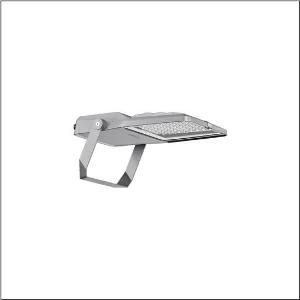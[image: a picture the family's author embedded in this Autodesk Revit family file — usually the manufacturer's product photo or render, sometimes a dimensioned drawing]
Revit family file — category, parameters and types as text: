
# Revit family: floodlight_fl_21_iq_mini___pl52_5xa7771d2d1a_936e
name_source: partatom
category: Lighting Fixtures
units: mm (PartAtom-declared; Revit-internal decimal feet)

## family parameters
Cut with Voids When Loaded = No
Host = Face
Light Source = No
Part Type = Normal
Room Calculation Point = No
Round Connector Dimension = Use Diameter
Shared = No

## types (1)
- --- (1 x LED, 17830 lm, 143 W, 3000K)
    Apparent Load = 143 VA
    CIE Flux Codes = 26 60 98 100 100
    Color Rendering = 70
    Color Temperature = 3000K
    Default Elevation = 1800 mm
    Description = Floodlight FL 21 iQ mini, floodlight, primary light control with lens, of PMMA, primary optical cover: protective disc, of toughened safety glass, transparent, light distribution: PL52, light emission: direct distribution, installation type: surface-mounted, LED, High Power LED, rated luminous flux: 17.830lm, luminous efficacy: 125lm/W, light colour: 730, colour temperature: 3000K, control: Auto-Match, Temp-Guard, Lumen-Switch, Night-Set, Smart-Wire, Light-Fading, Desk-Remote (wireless, voltage-free reading and setting of iQ features in the workshop via application-optimized NFC function/RFID function), optimised constant luminous flux control (CLO 2.0), with terminal, 6-pole, mains connection: 220..240V, AC, 50/60Hz, start of lifetime: 143W, end of service life: 152W, reduction: 61W, luminaire housing, of diecast aluminium, powder-coated, Siteco® metallic grey (DB 702S), corrosivity category C5 mid according to DIN EN ISO 12944, sealing non-destructively replaceable, mounting bracket, of steel, galvanised, powder-coated, Siteco® metallic grey (DB 702S), protection rating (complete): IP66, insulation class (complete): insulation class II (safety insulation), certification: CE, ENEC, VDE, protection symbol: D, impact resistance: IK08, permissible operating ambient temperature: -40..+40°C, permissible operating ambient temperature for outdoor applications: -40..+50°C, standard: DIN EN 12944, LABS conformity tested according to VDMA 24364:2018-05, packaging unit: 1 piece

Light Distribution: PL52
    Height = 70 mm
    Lamp = 1 x LED
    Lamp Light Flux = 17830 lm
    Lamp Power = 143 W
    Lamp count = 1
    Length = 485 mm
    Luminous efficacy = 125 lm/W
    Manufacturer = Siteco
    ModVariant = No
    Model = 5XA7771D2D1A
    Number of Poles = 1
    OnlyDefault = Yes
    Power Factor = 1
    Product Name = Floodlight FL 21 iQ mini | PL52
    Product group = floodlight | pylon annexe
    ProductGroupID = 6200
    Protection Class = Protection class II
    Protection Degree = IP 66
    RLX_Detail_Level = 1
    RLX_Emergency_Light_Flux = 0 lm
    RLX_Emergency_Type = 0
    RLX_Emergency_Type_DB = No
    RlxData = <blob elided: 96713 chars, md5=2ec7e221>
    Socket = socket
    Standby Power = 0 W
    System Light Flux = 17830 lm
    System Power = 143 W
    Type Comments = factory setting: luminous flux: 100 % | dim-lin: 254 | 730 mA
    Type Image = l_1006845.jpg
    URL = http://relux.com
    VarID = @adj_096353
    Voltage = 0 V
    Weight = 0.00 kg
    Width = 337 mm

## geometry (parser evidence)
native form markers: Blend x4, Sweep x11
no freeform markers — native parametric forms only
